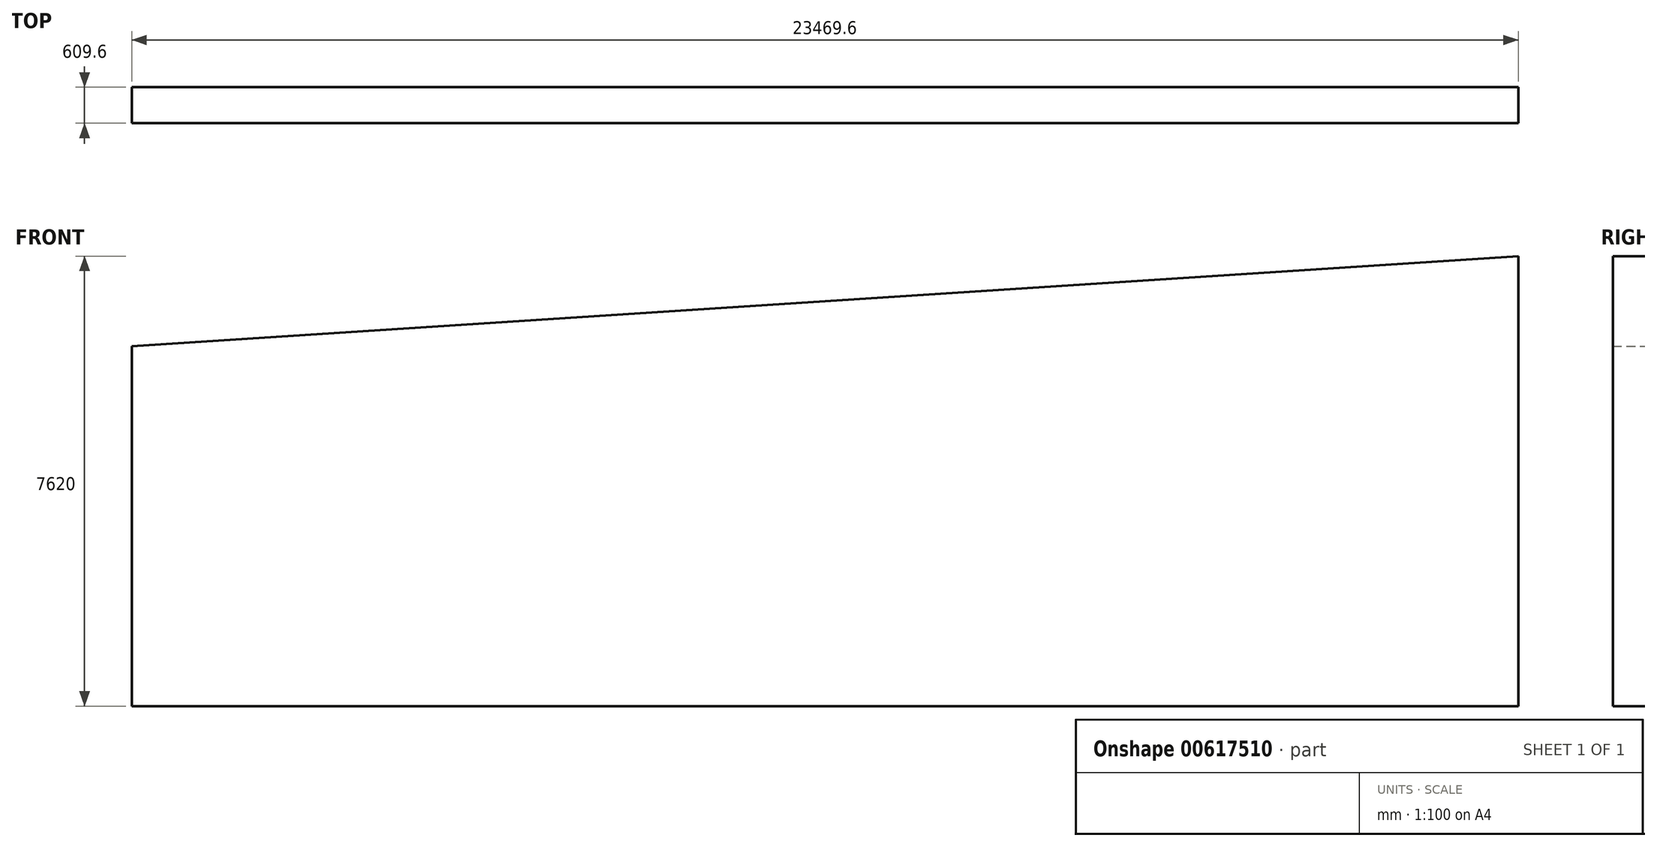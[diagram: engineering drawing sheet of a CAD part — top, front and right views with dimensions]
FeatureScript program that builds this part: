
annotation { "Feature Type Name" : "Feature", "Feature Type Description" : "" }
export const myFeature = defineFeature(function(context is Context, id is Id, definition is map)
    precondition{}
    {
        {
            var Q0;
            Q0=qCreatedBy(makeId("Front.planeOp"),FACE);
            var sketch = newSketch(context, id + "F0", { "sketchPlane" : qUnion([Q0])});
            skLineSegment(sketch, "E0.bottom", {"start": v(0, 0) * mm, "end": v(23469.6, 0) * mm});
            skLineSegment(sketch, "E0.left", {"start": v(0, 0) * mm, "end": v(0, 6096) * mm});
            skLineSegment(sketch, "E0.right", {"start": v(23469.6, 0) * mm, "end": v(23469.6, 7620) * mm});
            skLineSegment(sketch, "E1", {"start": v(0, 6096) * mm, "end": v(23469.6, 7620) * mm});
            skLineSegment(sketch, "E2.0", {"start": v(0, 6705.6) * mm, "end": v(23469.6, 6705.6) * mm});
            skLineSegment(sketch, "E3.1.0.0", {"start": v(22555.2, 0) * mm, "end": v(22555.2, 7620) * mm});
            skLineSegment(sketch, "E3.2.0.0", {"start": v(21640.8, 0) * mm, "end": v(21640.8, 7620) * mm});
            skLineSegment(sketch, "E3.3.0.0", {"start": v(20726.4, 0) * mm, "end": v(20726.4, 7620) * mm});
            skLineSegment(sketch, "E3.4.0.0", {"start": v(19812, 0) * mm, "end": v(19812, 7620) * mm});
            skLineSegment(sketch, "E3.5.0.0", {"start": v(18897.6, 0) * mm, "end": v(18897.6, 7620) * mm});
            skLineSegment(sketch, "E3.6.0.0", {"start": v(17983.2, 0) * mm, "end": v(17983.2, 7620) * mm});
            skLineSegment(sketch, "E3.7.0.0", {"start": v(17068.8, 0) * mm, "end": v(17068.8, 7620) * mm});
            skLineSegment(sketch, "E3.8.0.0", {"start": v(16154.4, 0) * mm, "end": v(16154.4, 7620) * mm});
            skLineSegment(sketch, "E3.9.0.0", {"start": v(15240, 0) * mm, "end": v(15240, 7620) * mm});
            skLineSegment(sketch, "E3.10.0.0", {"start": v(14325.6, 0) * mm, "end": v(14325.6, 7620) * mm});
            skLineSegment(sketch, "E3.11.0.0", {"start": v(13411.2, 0) * mm, "end": v(13411.2, 7620) * mm});
            skLineSegment(sketch, "E3.12.0.0", {"start": v(12496.8, 0) * mm, "end": v(12496.8, 7620) * mm});
            skLineSegment(sketch, "E3.13.0.0", {"start": v(11582.4, 0) * mm, "end": v(11582.4, 7620) * mm});
            skLineSegment(sketch, "E3.14.0.0", {"start": v(10668, 0) * mm, "end": v(10668, 7620) * mm});
            skLineSegment(sketch, "E3.15.0.0", {"start": v(9753.6, 0) * mm, "end": v(9753.6, 7620) * mm});
            skLineSegment(sketch, "E3.direction1", {"start": v(23469.6, 0) * mm, "end": v(22555.2, 0) * mm, "construction": true});
            skSolve(sketch);
        }
        {
            var Q0;
            Q0 = qSketchRegion(id + "F0", true);
            extrude(context, id + "F1", {"entities" : qUnion([Q0]), "depth" : 609.6 * mm, "offsetDistance" : 25.4 * mm});
        }
    });
